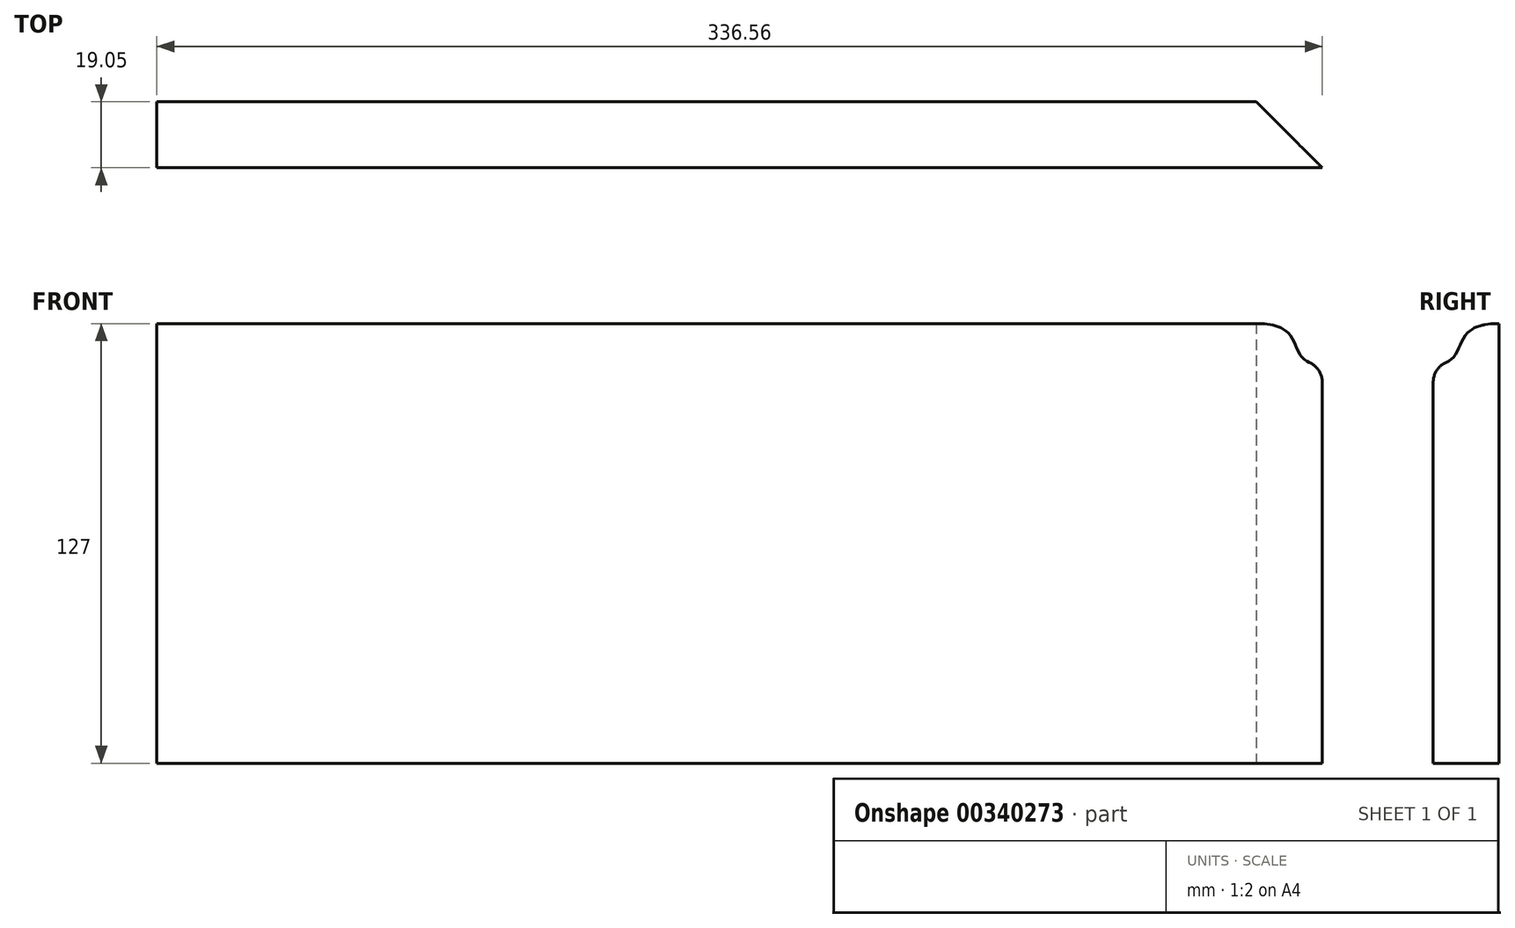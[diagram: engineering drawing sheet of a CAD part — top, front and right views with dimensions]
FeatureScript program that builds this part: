
annotation { "Feature Type Name" : "Feature", "Feature Type Description" : "" }
export const myFeature = defineFeature(function(context is Context, id is Id, definition is map)
    precondition{}
    {
        {
            var Q0;
            Q0=qCreatedBy(makeId("Front.planeOp"),FACE);
            var sketch = newSketch(context, id + "F0", { "sketchPlane" : qUnion([Q0])});
            skLineSegment(sketch, "E0.bottom", {"start": v(168.27, -63.5) * mm, "end": v(-168.28, -63.5) * mm});
            skLineSegment(sketch, "E0.top", {"start": v(168.27, 63.5) * mm, "end": v(-168.28, 63.5) * mm});
            skLineSegment(sketch, "E0.left", {"start": v(168.27, -63.5) * mm, "end": v(168.27, 63.5) * mm});
            skLineSegment(sketch, "E0.right", {"start": v(-168.28, -63.5) * mm, "end": v(-168.28, 63.5) * mm});
            skPoint(sketch, "E0.middle", {"position": v(0, 0) * mm});
            skSolve(sketch);
        }
        {
            var Q0;
            Q0=qSketchRegion(id+"F0",true);
            extrude(context, id + "F1", {"entities" : qUnion([Q0]), "depth" : 19.05 * mm});
        }
        {
            var Q0;
            Q0=makeQuery(id+"F1.opExtrude","SWEPT_FACE",FACE,{"disambiguationData":[OSD([sQuery(id+"F0.wireOp",EDGE,"E0.left")])]});
            var sketch = newSketch(context, id + "F2", { "sketchPlane" : qUnion([Q0])});
            skFitSpline(sketch, "E1", {"points": [v(0, 63.5) * mm, v(-19.05, 51.53) * mm], "startDerivative": vector(-48.08, 0) * mm, "endDerivative": vector(-35.63, -1.9) * mm});
            skArc(sketch, "E2.filletArc", {"start": v(-15.26, 52.32) * mm, "mid": v(-18.02, 49.98) * mm, "end": v(-19.05, 46.5) * mm});
            skLineSegment(sketch, "E3", {"start": v(0, 63.5) * mm, "end": v(-19.05, 63.5) * mm});
            skLineSegment(sketch, "E4", {"start": v(-19.05, 63.5) * mm, "end": v(-19.05, 46.5) * mm});
            skSolve(sketch);
        }
        {
            var Q0;
            Q0=qSketchRegion(id+"F2",true);
            extrude(context, id + "F3", {"entities" : qUnion([Q0]), "operationType" : NewBodyOperationType.REMOVE, "endBound" : BoundingType.THROUGH_ALL, "oppositeDirection" : true, "depth" : 25.4 * mm});
        }
        {
            var Q0;
            Q0=makeQuery(id+"F1.opExtrude","SWEPT_FACE",FACE,{"disambiguationData":[OSD([sQuery(id+"F0.wireOp",EDGE,"E0.bottom")])]});
            var sketch = newSketch(context, id + "F4", { "sketchPlane" : qUnion([Q0])});
            skLineSegment(sketch, "E5", {"start": v(0, 19.05) * mm, "end": v(0, 0) * mm, "construction": true});
            skLineSegment(sketch, "E6.MirrorCS", {"start": v(149.22, 0) * mm, "end": v(168.27, 19.05) * mm});
            skLineSegment(sketch, "E7.MirrorCS", {"start": v(168.27, 19.05) * mm, "end": v(168.27, 0) * mm});
            skLineSegment(sketch, "E8.MirrorCS", {"start": v(168.27, 0) * mm, "end": v(149.22, 0) * mm});
            skSolve(sketch);
        }
        {
            var Q0;
            Q0=qSketchRegion(id+"F4",true);
            extrude(context, id + "F5", {"entities" : qUnion([Q0]), "operationType" : NewBodyOperationType.REMOVE, "endBound" : BoundingType.THROUGH_ALL, "oppositeDirection" : true, "depth" : 25.4 * mm});
        }
    });
